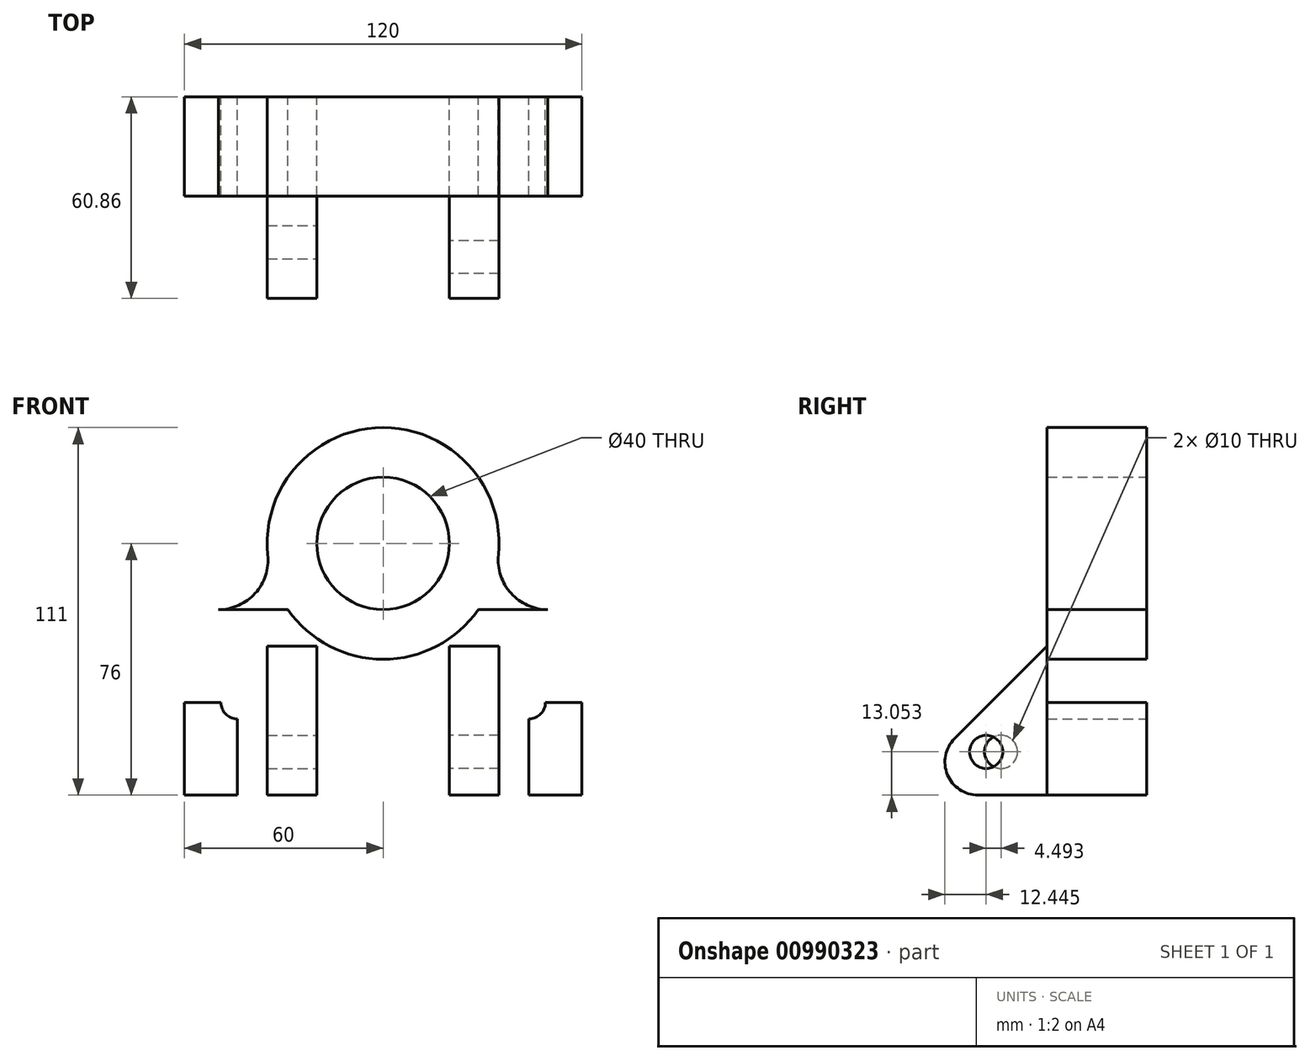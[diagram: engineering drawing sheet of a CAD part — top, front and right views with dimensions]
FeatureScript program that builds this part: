
annotation { "Feature Type Name" : "Feature", "Feature Type Description" : "" }
export const myFeature = defineFeature(function(context is Context, id is Id, definition is map)
    precondition{}
    {
        {
            var Q0;
            Q0=qCreatedBy(makeId("Front.planeOp"),FACE);
            var sketch = newSketch(context, id + "F0", { "sketchPlane" : qUnion([Q0])});
            skLineSegment(sketch, "E0.bottom", {"start": v(60, 28) * mm, "end": v(-60, 28) * mm});
            skLineSegment(sketch, "E0.top", {"start": v(60, -28) * mm, "end": v(-60, -28) * mm});
            skLineSegment(sketch, "E0.left", {"start": v(60, 28) * mm, "end": v(60, -28) * mm});
            skLineSegment(sketch, "E0.right", {"start": v(-60, 28) * mm, "end": v(-60, -28) * mm});
            skPoint(sketch, "E0.middle", {"position": v(0, 0) * mm});
            skCircle(sketch, "E1", {"center": v(0, 48) * mm, "radius": 20 * mm});
            skPoint(sketch, "E1.centerSnap0", {"position": v(0, 28) * mm});
            skCircle(sketch, "E2", {"center": v(0, 48) * mm, "radius": 35 * mm});
            skCircle(sketch, "E3", {"center": v(-49.75, 43) * mm, "radius": 15 * mm});
            skCircle(sketch, "E4", {"center": v(49.75, 43) * mm, "radius": 15 * mm});
            skLineSegment(sketch, "E5.bottom", {"start": v(-60, -28) * mm, "end": v(-44, -28) * mm});
            skLineSegment(sketch, "E5.top", {"start": v(-60, 0) * mm, "end": v(-44, 0) * mm});
            skLineSegment(sketch, "E5.left", {"start": v(-60, -28) * mm, "end": v(-60, 0) * mm});
            skLineSegment(sketch, "E5.right", {"start": v(-44, -28) * mm, "end": v(-44, 0) * mm});
            skLineSegment(sketch, "E6.bottom", {"start": v(60, -28) * mm, "end": v(44, -28) * mm});
            skLineSegment(sketch, "E6.top", {"start": v(60, 0) * mm, "end": v(44, 0) * mm});
            skLineSegment(sketch, "E6.left", {"start": v(60, -28) * mm, "end": v(60, 0) * mm});
            skLineSegment(sketch, "E6.right", {"start": v(44, -28) * mm, "end": v(44, 0) * mm});
            skCircle(sketch, "E7", {"center": v(-44, 0) * mm, "radius": 5 * mm});
            skCircle(sketch, "E8", {"center": v(44, 0) * mm, "radius": 5 * mm});
            skSolve(sketch);
        }
        {
            var Q0;
            Q0=makeQuery(id+"F0.imprint","IMPRINT",FACE,{"disambiguationData":[TD([[makeQuery(id+"F0.imprint","IMPRINT",EDGE,{"derivedFrom":sQuery(id+"F0.wireOp",EDGE,"E0.top")}),-1.0]])]});
            var Q1;
            {var subQ4=sQuery(id+"F0.wireOp",EDGE,"E1");Q1=makeQuery(id+"F0.imprint","IMPRINT",FACE,{"disambiguationData":[TD([[makeQuery(id+"F0.imprint","IMPRINT",EDGE,{"derivedFrom":subQ4}),-1.0]])]});}
            var Q2;
            {var subQ0=sQuery(id+"F0.wireOp",EDGE,"E0.bottom");var subQ1=makeQuery(id+"F0.imprint","INTERSECT",VERTEX,{"derivedFrom":[subQ0,sQuery(id+"F0.wireOp",EDGE,"E1")]});Q2=makeQuery(id+"F0.imprint","IMPRINT",FACE,{"disambiguationData":[TD([[makeQuery(id+"F0.imprint","IMPRINT",EDGE,{"disambiguationData":[TD([[subQ1,1.0]])],"derivedFrom":subQ0}),1.0]])]});}
            var Q3;
            {var subQ0=sQuery(id+"F0.wireOp",EDGE,"9b1R0ZDa-4O5S-ysr5-ctBU-q4yMMVBhA3CQ.right");Q3=makeQuery(id+"F0.imprint","IMPRINT",FACE,{"disambiguationData":[TD([[makeQuery(id+"F0.imprint","IMPRINT",EDGE,{"derivedFrom":subQ0}),1.0]])]});}
            var Q4;
            {var subQ0=sQuery(id+"F0.wireOp",EDGE,"vAGvdah1-dFaK-9A2N-NCVn-TFmRKkGsQoVQ.right");Q4=makeQuery(id+"F0.imprint","IMPRINT",FACE,{"disambiguationData":[TD([[makeQuery(id+"F0.imprint","IMPRINT",EDGE,{"derivedFrom":subQ0}),-1.0]])]});}
            var Q5;
            {var subQ0=sQuery(id+"F0.wireOp",EDGE,"E3");var subQ1=sQuery(id+"F0.wireOp",EDGE,"E0.bottom");var subQ2=makeQuery(id+"F0.imprint","INTERSECT",VERTEX,{"derivedFrom":[subQ1,subQ0]});Q5=makeQuery(id+"F0.imprint","IMPRINT",FACE,{"disambiguationData":[TD([[makeQuery(id+"F0.imprint","IMPRINT",EDGE,{"disambiguationData":[TD([[subQ2,1.0]])],"derivedFrom":subQ1}),-1.0]])]});}
            var Q6;
            {var subQ0=sQuery(id+"F0.wireOp",EDGE,"E4");var subQ1=sQuery(id+"F0.wireOp",EDGE,"E0.bottom");var subQ2=makeQuery(id+"F0.imprint","INTERSECT",VERTEX,{"derivedFrom":[subQ1,subQ0]});Q6=makeQuery(id+"F0.imprint","IMPRINT",FACE,{"disambiguationData":[TD([[makeQuery(id+"F0.imprint","IMPRINT",EDGE,{"disambiguationData":[TD([[subQ2,-1.0]])],"derivedFrom":subQ1}),-1.0]])]});}
            var Q7;
            {var subQ1=sQuery(id+"F0.wireOp",EDGE,"E5.bottom");Q7=makeQuery(id+"F0.imprint","IMPRINT",FACE,{"disambiguationData":[TD([[makeQuery(id+"F0.imprint","IMPRINT",EDGE,{"derivedFrom":subQ1}),1.0]])]});}
            var Q8;
            {var subQ1=sQuery(id+"F0.wireOp",EDGE,"E6.bottom");Q8=makeQuery(id+"F0.imprint","IMPRINT",FACE,{"disambiguationData":[TD([[makeQuery(id+"F0.imprint","IMPRINT",EDGE,{"derivedFrom":subQ1}),-1.0]])]});}
            extrude(context, id + "F1", {"entities" : qUnion([Q0, Q1, Q2, Q3, Q4, Q5, Q6, Q7, Q8]), "depth" : 30 * mm, "offsetDistance" : 25 * mm});
        }
        {
            var Q0;
            Q0=qCreatedBy(makeId("Right.planeOp"),FACE);
            cPlane(context, id + "F2", {"entities" : qUnion([Q0]), "cplaneType" : CPlaneType.OFFSET, "offset" : 20 * mm, "width" : 150 * mm, "height" : 150 * mm});
        }
        {
            var Q0;
            Q0=qCreatedBy(id+"F2.planeOp",FACE);
            var sketch = newSketch(context, id + "F3", { "sketchPlane" : qUnion([Q0])});
            skLineSegment(sketch, "E9", {"start": v(-30, -28) * mm, "end": v(-75, -28) * mm});
            skLineSegment(sketch, "E10", {"start": v(-30, -28) * mm, "end": v(-30, 17) * mm});
            skLineSegment(sketch, "E11", {"start": v(-30, 17) * mm, "end": v(-75, -28) * mm});
            skPoint(sketch, "E12", {"position": v(-48.41, -14.95) * mm});
            skCircle(sketch, "E13", {"center": v(-48.41, -14.95) * mm, "radius": 5 * mm});
            skSolve(sketch);
        }
        {
            var Q0;
            Q0=makeQuery(id+"F3.imprint","IMPRINT",FACE,{"disambiguationData":[TD([[makeQuery(id+"F3.imprint","IMPRINT",EDGE,{"derivedFrom":sQuery(id+"F3.wireOp",EDGE,"E9")}),-1.0]])]});
            extrude(context, id + "F4", {"entities" : qUnion([Q0]), "operationType" : NewBodyOperationType.ADD, "depth" : 15 * mm, "offsetDistance" : 25 * mm});
        }
        {
            var Q0;
            Q0=makeQuery(id+"F4.opExtrude","SWEPT_EDGE",EDGE,{"disambiguationData":[OSD([sQuery(id+"F3.wireOp",EDGE,"E9"),sQuery(id+"F3.wireOp",EDGE,"E11")])]});
            fillet(context, id + "F5", {"entities" : qUnion([Q0]), "radius" : 10 * mm, "tangentPropagation" : true, "allowEdgeOverflow" : false});
        }
        {
            var Q0;
            Q0=qCreatedBy(makeId("Right.planeOp"),FACE);
            cPlane(context, id + "F6", {"entities" : qUnion([Q0]), "cplaneType" : CPlaneType.OFFSET, "offset" : 20 * mm, "oppositeDirection" : true, "width" : 150 * mm, "height" : 150 * mm});
        }
        {
            var Q0;
            Q0=qCreatedBy(id+"F6.planeOp",FACE);
            var sketch = newSketch(context, id + "F7", { "sketchPlane" : qUnion([Q0])});
            skLineSegment(sketch, "E14", {"start": v(-30, -28) * mm, "end": v(-75, -28) * mm});
            skLineSegment(sketch, "E15", {"start": v(-30, -28) * mm, "end": v(-30, 17) * mm});
            skLineSegment(sketch, "E16", {"start": v(-30, 17) * mm, "end": v(-75, -28) * mm});
            skPoint(sketch, "E17", {"position": v(-43.92, -14.95) * mm});
            skCircle(sketch, "E18", {"center": v(-43.92, -14.95) * mm, "radius": 5 * mm});
            skSolve(sketch);
        }
        {
            var Q0;
            Q0=makeQuery(id+"F7.imprint","IMPRINT",FACE,{"disambiguationData":[TD([[makeQuery(id+"F7.imprint","IMPRINT",EDGE,{"derivedFrom":sQuery(id+"F7.wireOp",EDGE,"E14")}),-1.0]])]});
            extrude(context, id + "F8", {"entities" : qUnion([Q0]), "oppositeDirection" : true, "depth" : 15 * mm, "offsetDistance" : 25 * mm});
        }
        {
            var Q0;
            Q0=makeQuery(id+"F8.opExtrude","SWEPT_EDGE",EDGE,{"disambiguationData":[OSD([sQuery(id+"F7.wireOp",EDGE,"E14"),sQuery(id+"F7.wireOp",EDGE,"E16")])]});
            fillet(context, id + "F9", {"entities" : qUnion([Q0]), "radius" : 10 * mm, "tangentPropagation" : true, "allowEdgeOverflow" : false});
        }
    });
